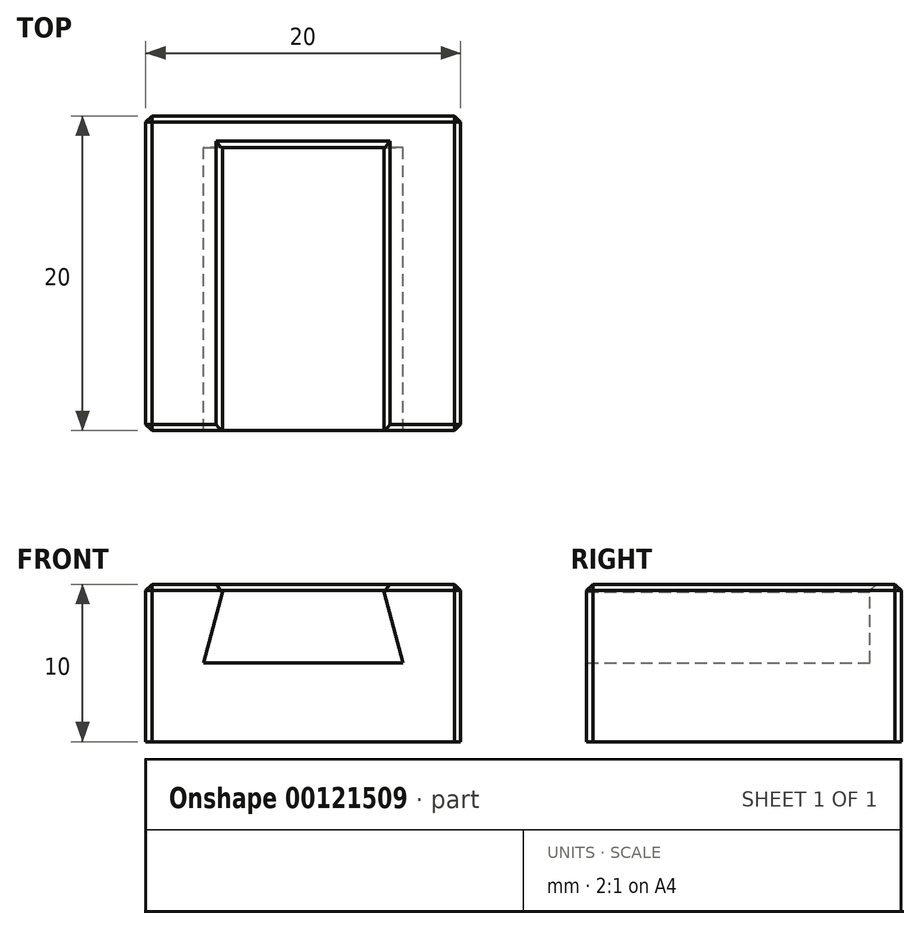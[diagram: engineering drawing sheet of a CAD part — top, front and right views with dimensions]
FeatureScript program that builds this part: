
annotation { "Feature Type Name" : "Feature", "Feature Type Description" : "" }
export const myFeature = defineFeature(function(context is Context, id is Id, definition is map)
    precondition{}
    {
        {
            assignVariable(context, id + "F0", {"name" : "PrintOffset", "anyValue" : 0.4});
        }
        {
            assignVariable(context, id + "F1", {"name" : "DovetailBackstopDepth", "anyValue" : 2});
        }
        {
            assignVariable(context, id + "F2", {"name" : "DovetailDepth", "anyValue" : 20});
        }
        {
            var Q0;
            Q0=qCreatedBy(makeId("Front.planeOp"),FACE);
            var sketch = newSketch(context, id + "F3", { "sketchPlane" : qUnion([Q0])});
            skLineSegment(sketch, "E0", {"start": v(-10, 0) * mm, "end": v(10, 0) * mm});
            skLineSegment(sketch, "E1", {"start": v(-10, 0) * mm, "end": v(-10, 10) * mm});
            skLineSegment(sketch, "E2", {"start": v(-10, 10) * mm, "end": v(-5, 10) * mm});
            skLineSegment(sketch, "E3", {"start": v(-5, 10) * mm, "end": v(-6.34, 5) * mm});
            skLineSegment(sketch, "E4", {"start": v(-6.34, 5) * mm, "end": v(6.34, 5) * mm});
            skLineSegment(sketch, "E5", {"start": v(6.34, 5) * mm, "end": v(5, 10) * mm});
            skLineSegment(sketch, "E6", {"start": v(5, 10) * mm, "end": v(10, 10) * mm});
            skLineSegment(sketch, "E7", {"start": v(10, 10) * mm, "end": v(10, 0) * mm});
            skPoint(sketch, "E8", {"position": v(0, 5) * mm});
            skLineSegment(sketch, "E9", {"start": v(-5, 10) * mm, "end": v(5, 10) * mm});
            skSolve(sketch);
        }
        {
            var Q0;
            Q0=makeQuery(id+"F3.imprint","IMPRINT",FACE,{"disambiguationData":[TD([[makeQuery(id+"F3.imprint","IMPRINT",EDGE,{"derivedFrom":sQuery(id+"F3.wireOp",EDGE,"E0")}),1.0]])]});
            extrude(context, id + "F4", {"entities" : qUnion([Q0]), "depth" : (getVariable(context, 'DovetailDepth')) * mm});
        }
        {
            var Q0;
            Q0=makeQuery(id+"F3.imprint","IMPRINT",FACE,{"disambiguationData":[TD([[makeQuery(id+"F3.imprint","IMPRINT",EDGE,{"derivedFrom":sQuery(id+"F3.wireOp",EDGE,"E3")}),1.0]])]});
            extrude(context, id + "F5", {"entities" : qUnion([Q0]), "operationType" : NewBodyOperationType.ADD, "depth" : (getVariable(context, 'DovetailBackstopDepth')) * mm});
        }
        {
            var Q0;
            Q0=makeQuery(id+"F4.opExtrude","CAP_EDGE",EDGE,{"disambiguationData":[OSD([sQuery(id+"F3.wireOp",EDGE,"E1")])],"isStart":false});
            var Q1;
            Q1=makeQuery(id+"F4.opExtrude","CAP_EDGE",EDGE,{"disambiguationData":[OSD([sQuery(id+"F3.wireOp",EDGE,"E7")])],"isStart":false});
            var Q2;
            Q2=makeQuery(id+"F4.opExtrude","CAP_EDGE",EDGE,{"disambiguationData":[OSD([sQuery(id+"F3.wireOp",EDGE,"E7")])],"isStart":true});
            var Q3;
            Q3=makeQuery(id+"F4.opExtrude","CAP_EDGE",EDGE,{"disambiguationData":[OSD([sQuery(id+"F3.wireOp",EDGE,"E1")])],"isStart":true});
            var Q4;
            Q4=makeQuery(id+"F5.boolean.opBoolean","MERGE",EDGE,{"derivedFrom":[makeQuery(id+"F4.opExtrude","CAP_EDGE",EDGE,{"disambiguationData":[OSD([sQuery(id+"F3.wireOp",EDGE,"E2")])],"isStart":true}),makeQuery(id+"F4.opExtrude","CAP_EDGE",EDGE,{"disambiguationData":[OSD([sQuery(id+"F3.wireOp",EDGE,"E6")])],"isStart":true}),makeQuery(id+"F5.opExtrude","CAP_EDGE",EDGE,{"disambiguationData":[OSD([sQuery(id+"F3.wireOp",EDGE,"E9")])],"isStart":true})]});
            var Q5;
            Q5=makeQuery(id+"F4.opExtrude","SWEPT_EDGE",EDGE,{"disambiguationData":[OSD([sQuery(id+"F3.wireOp",EDGE,"E1"),sQuery(id+"F3.wireOp",EDGE,"E2")])]});
            var Q6;
            Q6=makeQuery(id+"F4.opExtrude","SWEPT_EDGE",EDGE,{"disambiguationData":[OSD([sQuery(id+"F3.wireOp",EDGE,"E6"),sQuery(id+"F3.wireOp",EDGE,"E7")])]});
            var Q7;
            Q7=makeQuery(id+"F4.opExtrude","CAP_EDGE",EDGE,{"disambiguationData":[OSD([sQuery(id+"F3.wireOp",EDGE,"E2")])],"isStart":false});
            var Q8;
            Q8=makeQuery(id+"F4.opExtrude","CAP_EDGE",EDGE,{"disambiguationData":[OSD([sQuery(id+"F3.wireOp",EDGE,"E6")])],"isStart":false});
            var Q9;
            Q9=makeQuery(id+"F4.opExtrude","SWEPT_EDGE",EDGE,{"disambiguationData":[OSD([sQuery(id+"F3.wireOp",EDGE,"E2"),sQuery(id+"F3.wireOp",EDGE,"E3"),sQuery(id+"F3.wireOp",EDGE,"E9")])]});
            var Q10;
            Q10=makeQuery(id+"F5.opExtrude","CAP_EDGE",EDGE,{"disambiguationData":[OSD([sQuery(id+"F3.wireOp",EDGE,"E9")])],"isStart":false});
            var Q11;
            Q11=makeQuery(id+"F4.opExtrude","SWEPT_EDGE",EDGE,{"disambiguationData":[OSD([sQuery(id+"F3.wireOp",EDGE,"E5"),sQuery(id+"F3.wireOp",EDGE,"E6"),sQuery(id+"F3.wireOp",EDGE,"E9")])]});
            chamfer(context, id + "F6", {"entities" : qUnion([Q0, Q1, Q2, Q3, Q4, Q5, Q6, Q7, Q8, Q9, Q10, Q11]), "width" : (getVariable(context, 'PrintOffset')) * mm, "tangentPropagation" : true});
        }
    });
